# Revit family: 873-00-002-DN900-1000
name_source: partatom
category: Generic Models
units: mm (PartAtom-declared; Revit-internal decimal feet)

## family parameters
Always vertical = Yes
Can host rebar = No
Cut with Voids When Loaded = No
Part Type = Normal
Room Calculation Point = No
Round Connector Dimension = Use Diameter
Shared = No
Work Plane-Based = No

## types (2) — shared parameters
873-0900-00-741000 = DN900_PN25
873-1000-00-741000 = DN1000_PN25
Angle = 22.50°
Body_Wallthicknss = 10 mm  [stored 0.0328084 ft]
Description_ = AVK DISMANTLING JOINT
Flange_thickness = 20 mm  [stored 0.0656168 ft]
Search_table = 873-00-002-DN900-1000
URL product pages = https://www.avkvalves.com

## per-type parameters (varying)
| type | A | DN | Id(Radius) | L | T | d1 | d2 |
| DN0900 | 355 mm | 900 mm  [stored 2.95276 ft] | 450 mm  [stored 1.47638 ft] | 620 mm  [stored 2.03412 ft] | 45 mm  [stored 0.147638 ft] | 1090 mm  [stored 3.57612 ft] | 593 mm |
| DN1000 | 375 mm  [stored 1.23031 ft] | 1000 mm  [stored 3.28084 ft] | 500 mm  [stored 1.64042 ft] | 660 mm  [stored 2.16535 ft] | 52 mm | 1210 mm  [stored 3.96982 ft] | 660 mm  [stored 2.16535 ft] |

note: [stored X ft] marks values corroborated as IEEE doubles in the binary element streams (Revit-internal decimal feet)

## geometry (parser evidence)
native form markers: Sweep x5
no freeform markers — native parametric forms only
